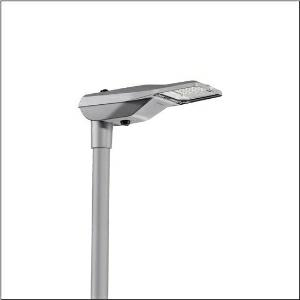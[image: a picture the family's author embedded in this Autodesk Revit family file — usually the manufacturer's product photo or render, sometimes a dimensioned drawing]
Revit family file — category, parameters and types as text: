
# Revit family: streetlight_sl_21_iq_micro___st1_0a_5xe1d41y08cb_9909
name_source: partatom
category: Lighting Fixtures
units: mm (PartAtom-declared; Revit-internal decimal feet)

## family parameters
Cut with Voids When Loaded = No
Host = Face
Light Source = No
Part Type = Normal
Room Calculation Point = No
Round Connector Dimension = Use Diameter
Shared = No

## types (1)
- --- (1 x LED, 2970 lm, 19.1 W, 4000K)
    Apparent Load = 19 VA
    CIE Flux Codes = 37 72 97 100 100
    Color Rendering = 70
    Color Temperature = 4000K
    Default Elevation = 1800 mm
    Description = Streetlight SL 21 iQ micro, mast luminaire, primary light control with lens, of PMMA, primary optical cover: cover, of toughened safety glass, transparent, light distribution: ST1.0a, light emission: direct distribution, primary light characteristic: asymmetric, installation type: post-top, side-entry, LED, High Power LED, rated luminous flux: 2.970lm, luminous efficacy: 156lm/W, light colour: 740, colour temperature: 4000K, control gear: iQ-Street Remote, D4i with power reduction, control: pre-setting: logarithmic dimming characteristic, Street-Remote, Auto-Match, Temp-Guard, Lumen-Switch, Night-Set, Smart-Wire, Light-Fading, Desk-Remote (wireless, voltage-free reading and setting of iQ features in the workshop via application-optimized NFC function/RFID function), optimised constant luminous flux control (CLO 2.0), mains connection: 220..240V, AC, 50/60Hz, start of lifetime: 19W, end of service life: 20W, reduction: 9W, luminaire housing, of diecast aluminium, powder-coated, Siteco® metallic grey (DB 702S), corrosivity category C5 mid according to DIN EN ISO 12944, please order mast flange separately, inclination adjustable: 0°, 5°, 10°, 15°, sealing non-destructively replaceable, multi-level sealing system, length: 528mm, width: 235mm, height: 110mm, mast flange for spigot size: 42mm (side-entry): 5XC10008XM4, 60/48mm (side-entry/post-top): 5XC10108XM2, 76/60mm (side-entry/post-top): 5XC10108XM1, mounting height: 4..8m, Smart Interface below and above, protection rating (complete): IP66, insulation class (complete): insulation class II (safety insulation), certification: CE, ENEC, ENEC+, VDE, impact resistance: IK10, permissible operating ambient temperature for outdoor applications: -40..+50°C, standard-compliant lighting for roads and squares, packaging unit: 1 piece

Light Distribution: ST1.0a
    Height = 110 mm
    Lamp = 1 x LED
    Lamp Light Flux = 2970 lm
    Lamp Power = 19.1 W
    Lamp count = 1
    Length = 528 mm
    Luminous efficacy = 156 lm/W
    Manufacturer = Siteco
    ModVariant = No
    Model = 5XE1D41Y08CB
    Number of Poles = 1
    OnlyDefault = Yes
    Power Factor = 1
    Product Name = Streetlight SL 21 iQ micro | ST1.0a
    Product group = mast luminaire | pylon top
    ProductGroupID = 6100
    Protection Class = Protection class II
    Protection Degree = IP 66
    RLX_Detail_Level = 1
    RLX_Emergency_Light_Flux = 0 lm
    RLX_Emergency_Type = 0
    RLX_Emergency_Type_DB = No
    RlxData = <blob elided: 99033 chars, md5=81c94b5a>
    Socket = socket
    Standby Power = 0 W
    System Light Flux = 2970 lm
    System Power = 19 W
    Type Comments = factory setting: luminous flux: 100 % | dim-lin: 254 | 387 mA
    Type Image = l_1007239.jpg
    URL = http://relux.com
    VarID = @adj_136781
    Voltage = 0 V
    Weight = 0.00 kg
    Width = 235 mm

## geometry (parser evidence)
native form markers: Blend x4, Sweep x12
no freeform markers — native parametric forms only
